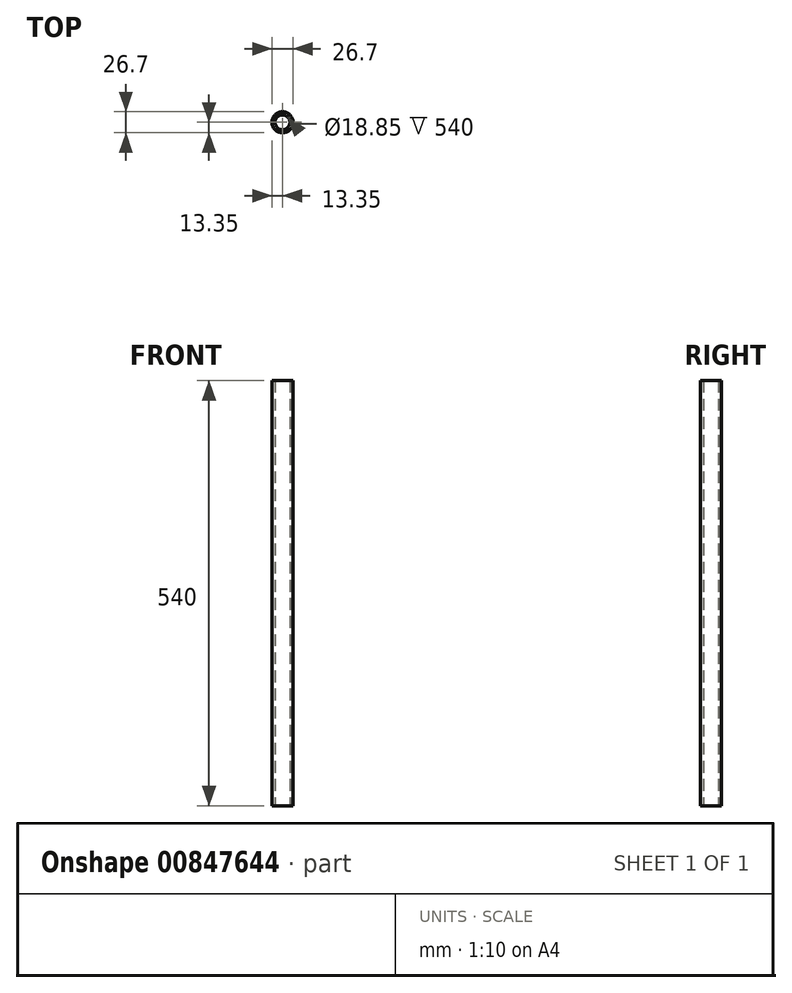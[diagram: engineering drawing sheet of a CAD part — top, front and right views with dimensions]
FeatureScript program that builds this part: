
annotation { "Feature Type Name" : "Feature", "Feature Type Description" : "" }
export const myFeature = defineFeature(function(context is Context, id is Id, definition is map)
    precondition{}
    {
        {
            var Q0;
            Q0=qCreatedBy(makeId("Top.planeOp"),FACE);
            var sketch = newSketch(context, id + "F0", { "sketchPlane" : qUnion([Q0])});
            skCircle(sketch, "E0", {"center": v(0, 0) * mm, "radius": 9.42 * mm});
            skCircle(sketch, "E1", {"center": v(0, 0) * mm, "radius": 13.35 * mm});
            skSolve(sketch);
        }
        {
            var Q0;
            Q0=makeQuery(id+"F0.imprint","IMPRINT",FACE,{"disambiguationData":[TD([[makeQuery(id+"F0.imprint","IMPRINT",EDGE,{"derivedFrom":sQuery(id+"F0.wireOp",EDGE,"E0")}),-1.0]])]});
            extrude(context, id + "F1", {"entities" : qUnion([Q0]), "depth" : 540 * mm, "offsetDistance" : 25 * mm});
        }
    });
